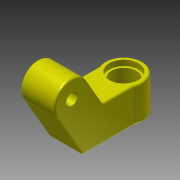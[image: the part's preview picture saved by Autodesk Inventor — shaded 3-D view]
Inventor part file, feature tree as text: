
AUTODESK INVENTOR PART (.ipt)
format: ipt  version: 2013 (Build 170138000, 138)  size: 201,216 bytes
history: native  units: mm
features: extrude x7, sketch x7, chamfer x1, fillet x1
ambient origin geometry x8: Origin, YZ Plane, XZ Plane, XY Plane, X Axis, Y Axis, Z Axis, Center Point
bodies: Solid1 (feature_tree)
feature tree (16):
  extrude  "Extrusion1"  Depth=50.0mm
  extrude  "Extrusion2"  Depth=25.0mm
  extrude  "Extrusion12"  Depth=25.0mm TaperAngle=0.0deg
  extrude  "Extrusion13"  TaperAngle=120.0deg  [1 undecoded]
  extrude  "Extrusion14"  Depth=6.0mm TaperAngle=0.0deg
  extrude  "Extrusion15"  Depth=6.0mm TaperAngle=0.0deg
  chamfer  "Chamfer4"  Distance=4.0mm
  extrude  "Extrusion16"  Depth=21.1mm
  fillet  "Fillet2"  Radius=4.0mm
  sketch  "Sketch1"  dims[d0=8.1mm d2=50.0mm]
  sketch  "Sketch2"  dims[d3=14.0mm d4=25.0mm]
  sketch  "Sketch12"  dims[d6=25.0mm d7=25.0mm d8=0.0mm]
  sketch  "Sketch13"  dims[d9=25.0mm d10=0.0mm d40=120.0deg]
  sketch  "Sketch14"  dims[d56=13.1mm d57=6.0mm d58=0.0mm]
  sketch  "Sketch15"  dims[d59=18.1mm d61=6.0mm d62=0.0mm]
  sketch  "Sketch16"  dims[d63=21.1mm d65=4.0mm d66=0.0mm d67=21.1mm d69=4.0mm d70=0.0mm d72=1.5mm d73=2.0mm d74=45.0deg d76=3.0mm d77=10.0mm d78=0.0mm d79=1.5mm]
note: 1 required parameter value undecoded (feature->parameter linkage not recoverable at this tier; creation-order binding heuristic only, values carry confidence <= 0.55)
